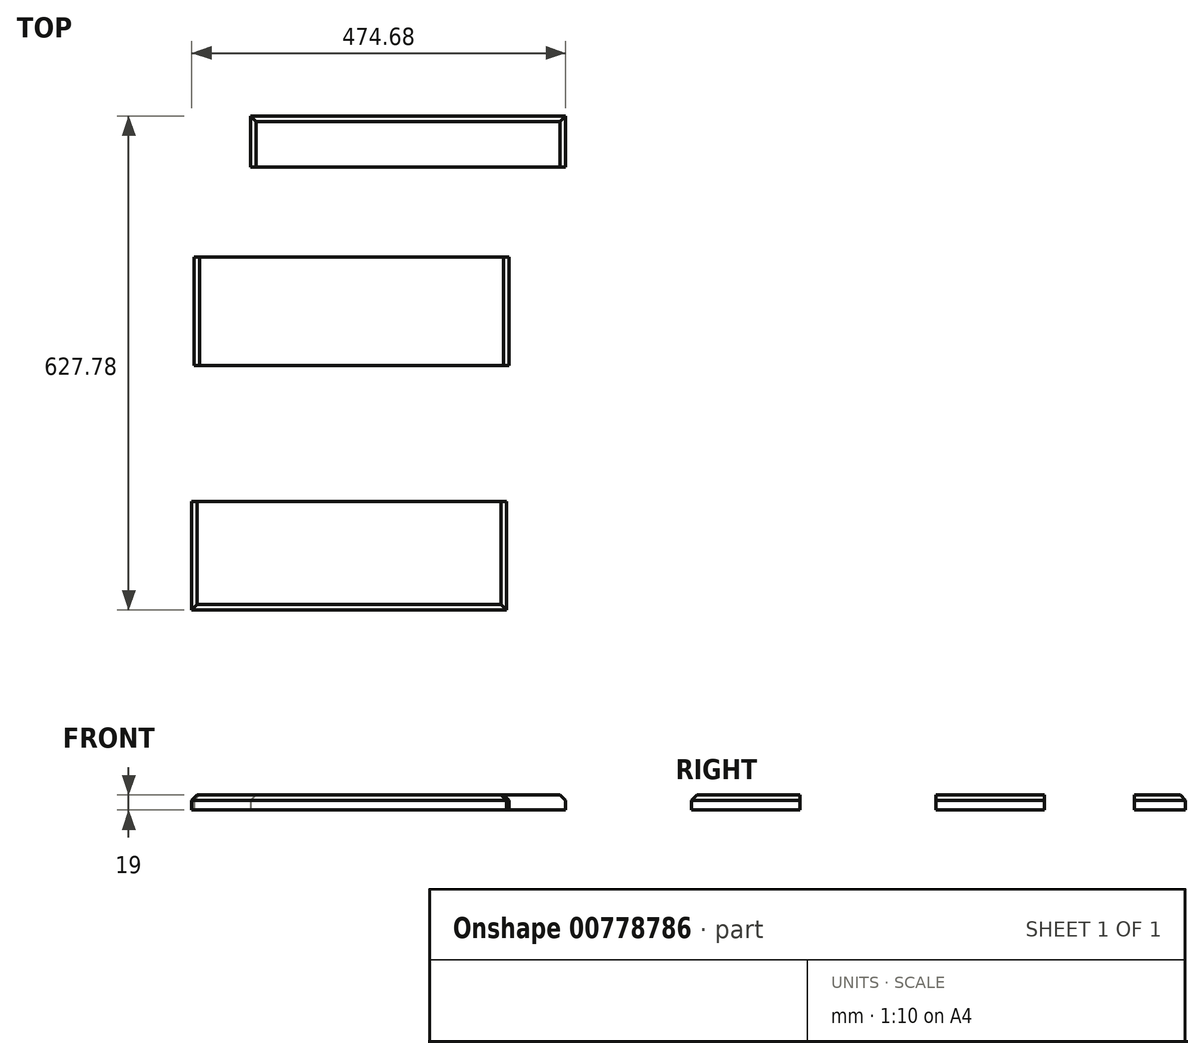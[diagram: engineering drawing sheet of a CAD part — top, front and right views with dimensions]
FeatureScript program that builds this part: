
annotation { "Feature Type Name" : "Feature", "Feature Type Description" : "" }
export const myFeature = defineFeature(function(context is Context, id is Id, definition is map)
    precondition{}
    {
        {
            var Q0;
            Q0=qCreatedBy(makeId("Top.planeOp"),FACE);
            var sketch = newSketch(context, id + "F0", { "sketchPlane" : qUnion([Q0])});
            skLineSegment(sketch, "E0.bottom", {"start": v(-208.88, -94.27) * mm, "end": v(191.12, -94.27) * mm});
            skLineSegment(sketch, "E0.top", {"start": v(-208.88, -232.27) * mm, "end": v(191.12, -232.27) * mm});
            skLineSegment(sketch, "E0.left", {"start": v(-208.88, -94.27) * mm, "end": v(-208.88, -232.27) * mm});
            skLineSegment(sketch, "E0.right", {"start": v(191.12, -94.27) * mm, "end": v(191.12, -232.27) * mm});
            skSolve(sketch);
        }
        {
            var Q0;
            Q0=makeQuery(id+"F0.imprint","IMPRINT",FACE,{"disambiguationData":[TD([[makeQuery(id+"F0.imprint","IMPRINT",EDGE,{"derivedFrom":sQuery(id+"F0.wireOp",EDGE,"E0.bottom")}),-1.0]])]});
            extrude(context, id + "F1", {"entities" : qUnion([Q0]), "depth" : 19 * mm, "offsetDistance" : 25 * mm});
        }
        {
            var Q0;
            Q0=qCreatedBy(makeId("Top.planeOp"),FACE);
            var sketch = newSketch(context, id + "F2", { "sketchPlane" : qUnion([Q0])});
            skLineSegment(sketch, "E1.bottom", {"start": v(-137.13, 84.96) * mm, "end": v(262.87, 84.96) * mm});
            skLineSegment(sketch, "E1.top", {"start": v(-137.13, 19.96) * mm, "end": v(262.87, 19.96) * mm});
            skLineSegment(sketch, "E1.left", {"start": v(-137.13, 84.96) * mm, "end": v(-137.13, 19.96) * mm});
            skLineSegment(sketch, "E1.right", {"start": v(262.87, 84.96) * mm, "end": v(262.87, 19.96) * mm});
            skSolve(sketch);
        }
        {
            var Q0;
            Q0=makeQuery(id+"F2.imprint","IMPRINT",FACE,{"disambiguationData":[TD([[makeQuery(id+"F2.imprint","IMPRINT",EDGE,{"derivedFrom":sQuery(id+"F2.wireOp",EDGE,"E1.bottom")}),-1.0]])]});
            extrude(context, id + "F3", {"entities" : qUnion([Q0]), "depth" : 19 * mm, "offsetDistance" : 25 * mm});
        }
        {
            var Q0;
            Q0=qCreatedBy(makeId("Top.planeOp"),FACE);
            var sketch = newSketch(context, id + "F4", { "sketchPlane" : qUnion([Q0])});
            skLineSegment(sketch, "E2.bottom", {"start": v(-211.8, -404.82) * mm, "end": v(188.2, -404.82) * mm});
            skLineSegment(sketch, "E2.top", {"start": v(-211.8, -542.82) * mm, "end": v(188.2, -542.82) * mm});
            skLineSegment(sketch, "E2.left", {"start": v(-211.8, -404.82) * mm, "end": v(-211.8, -542.82) * mm});
            skLineSegment(sketch, "E2.right", {"start": v(188.2, -404.82) * mm, "end": v(188.2, -542.82) * mm});
            skSolve(sketch);
        }
        {
            var Q0;
            Q0 = qSketchRegion(id + "F4", true);
            extrude(context, id + "F5", {"entities" : qUnion([Q0]), "depth" : 19 * mm, "offsetDistance" : 25 * mm});
        }
        {
            var Q0;
            Q0=makeQuery(id+"F5.opExtrude","CAP_EDGE",EDGE,{"disambiguationData":[OSD([sQuery(id+"F4.wireOp",EDGE,"E2.top")])],"isStart":false});
            var Q1;
            Q1=makeQuery(id+"F5.opExtrude","CAP_EDGE",EDGE,{"disambiguationData":[OSD([sQuery(id+"F4.wireOp",EDGE,"E2.left")])],"isStart":false});
            var Q2;
            Q2=makeQuery(id+"F5.opExtrude","CAP_EDGE",EDGE,{"disambiguationData":[OSD([sQuery(id+"F4.wireOp",EDGE,"E2.right")])],"isStart":false});
            chamfer(context, id + "F6", {"entities" : qUnion([Q0, Q1, Q2]), "width" : 7 * mm, "tangentPropagation" : true});
        }
        {
            var Q0;
            Q0=makeQuery(id+"F1.opExtrude","CAP_EDGE",EDGE,{"disambiguationData":[OSD([sQuery(id+"F0.wireOp",EDGE,"E0.left")])],"isStart":false});
            var Q1;
            Q1=makeQuery(id+"F1.opExtrude","CAP_EDGE",EDGE,{"disambiguationData":[OSD([sQuery(id+"F0.wireOp",EDGE,"E0.right")])],"isStart":false});
            chamfer(context, id + "F7", {"entities" : qUnion([Q0, Q1]), "width" : 7 * mm, "tangentPropagation" : true});
        }
        {
            var Q0;
            Q0=makeQuery(id+"F3.opExtrude","CAP_EDGE",EDGE,{"disambiguationData":[OSD([sQuery(id+"F2.wireOp",EDGE,"E1.left")])],"isStart":false});
            var Q1;
            Q1=makeQuery(id+"F3.opExtrude","CAP_EDGE",EDGE,{"disambiguationData":[OSD([sQuery(id+"F2.wireOp",EDGE,"E1.bottom")])],"isStart":false});
            var Q2;
            Q2=makeQuery(id+"F3.opExtrude","CAP_EDGE",EDGE,{"disambiguationData":[OSD([sQuery(id+"F2.wireOp",EDGE,"E1.right")])],"isStart":false});
            chamfer(context, id + "F8", {"entities" : qUnion([Q0, Q1, Q2]), "width" : 7 * mm, "tangentPropagation" : true});
        }
    });
